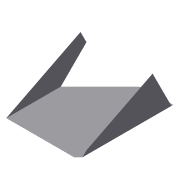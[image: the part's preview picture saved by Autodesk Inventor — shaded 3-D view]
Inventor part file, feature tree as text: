
AUTODESK INVENTOR PART (.ipt)
format: ipt  version: 2016 (Build 200138000, 138)  size: 147,968 bytes
history: native  units: mm
features: sheet_metal_op x6, sketch x4, other x2
ambient origin geometry x8: Origin, YZ Plane, XZ Plane, XY Plane, X Axis, Y Axis, Z Axis, Center Point
bodies: Body1 (feature_tree)
feature tree (12):
  sheet_metal_op  "Face4"
  sheet_metal_op  "Fold5"
  sheet_metal_op  "Fold6"
  sheet_metal_op  "Flange2"
  sketch  "Sketch10"  dims[d2=0.5mm]
  other  "Plate5"
  sketch  "Sketch11"  dims[d20=0.5mm]
  sketch  "Sketch12"  dims[d40=0.5mm]
  sketch  "Sketch13"  dims[d55=800.0mm d56=619.0mm d57=360.0mm d58=90.0deg d59=360.0mm d60=0.5mm d61=0.5mm d62=0.25mm d63=1.0mm d64=0.5mm d65=90.0deg d66=0.5mm d67=0.5mm d68=0.25mm d69=1.0mm d70=0.5mm d71=90.0deg d72=0.5mm d73=0.5mm d74=0.25mm d75=1.0mm d76=0.5mm d77=20.0mm d78=-1.745329mm d79=0.5mm d80=2.0mm d81=0.5mm d82=0.5mm]
  other  "Plate6"
  sheet_metal_op  "Bend2"
  sheet_metal_op  "Corner2"
